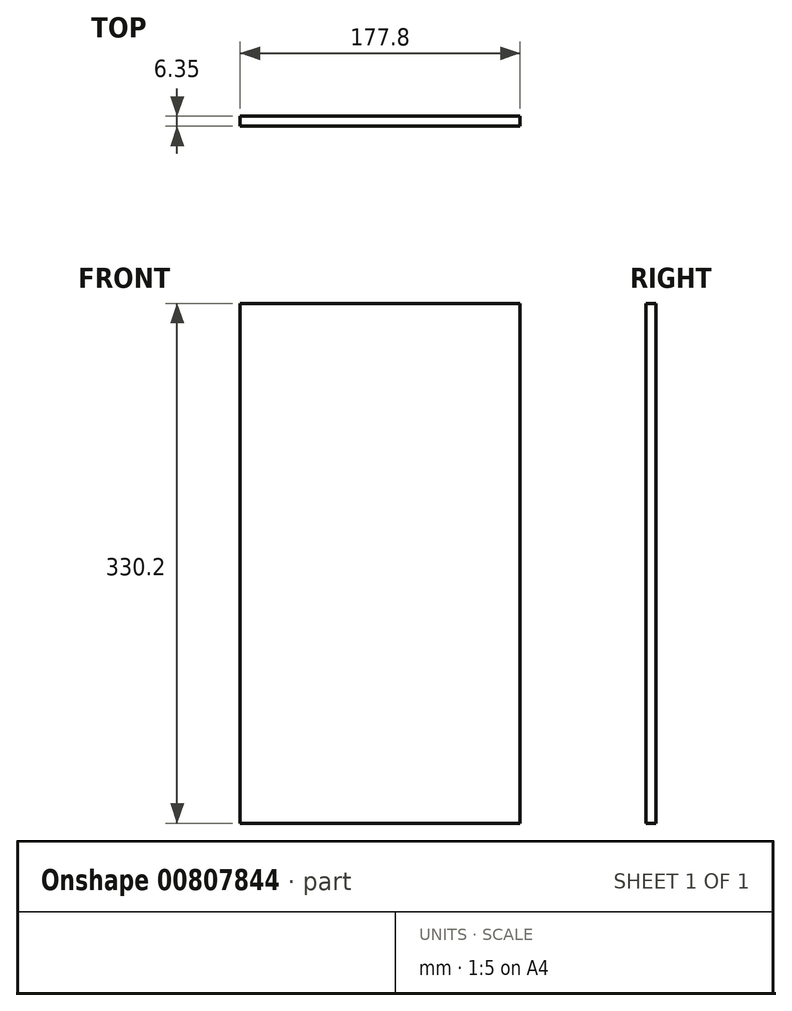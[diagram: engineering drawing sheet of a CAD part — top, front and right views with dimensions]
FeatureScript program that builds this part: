
annotation { "Feature Type Name" : "Feature", "Feature Type Description" : "" }
export const myFeature = defineFeature(function(context is Context, id is Id, definition is map)
    precondition{}
    {
        {
            var Q0;
            Q0=qCreatedBy(makeId("Front.planeOp"),FACE);
            var sketch = newSketch(context, id + "F0", { "sketchPlane" : qUnion([Q0])});
            skLineSegment(sketch, "E0.bottom", {"start": v(-86.63, 237.69) * mm, "end": v(91.17, 237.69) * mm});
            skLineSegment(sketch, "E0.top", {"start": v(-86.63, -92.51) * mm, "end": v(91.17, -92.51) * mm});
            skLineSegment(sketch, "E0.left", {"start": v(-86.63, 237.69) * mm, "end": v(-86.63, -92.51) * mm});
            skLineSegment(sketch, "E0.right", {"start": v(91.17, 237.69) * mm, "end": v(91.17, -92.51) * mm});
            skSolve(sketch);
        }
        {
            var Q0;
            Q0 = qSketchRegion(id + "F0", true);
            extrude(context, id + "F1", {"entities" : qUnion([Q0]), "depth" : 6.35 * mm, "offsetDistance" : 25.4 * mm});
        }
    });
